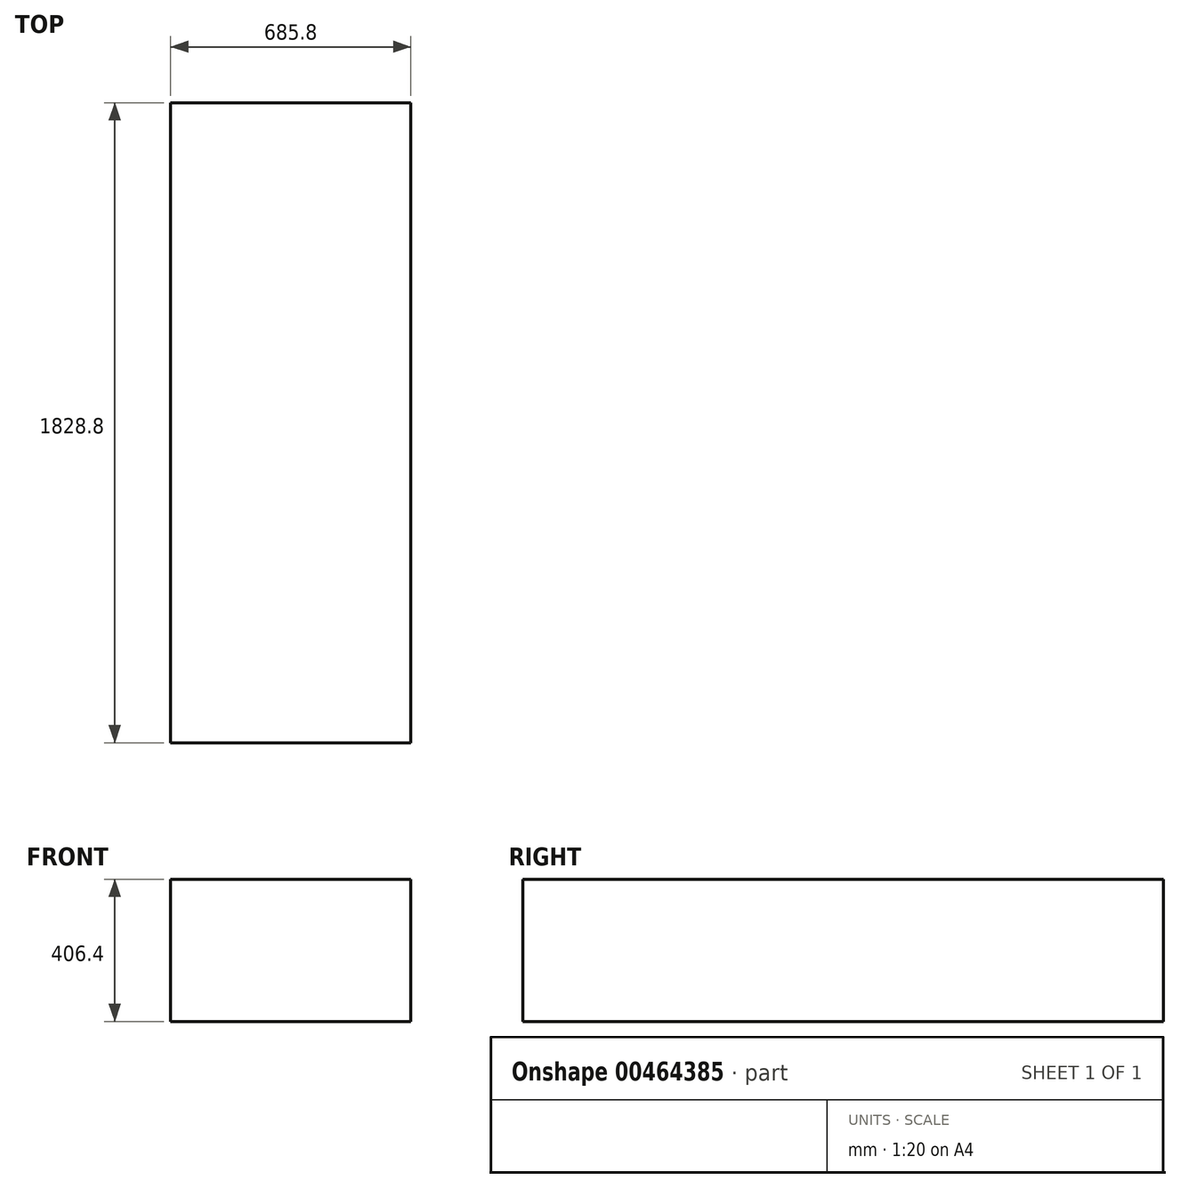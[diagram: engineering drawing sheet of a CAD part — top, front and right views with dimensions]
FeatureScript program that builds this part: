
annotation { "Feature Type Name" : "Feature", "Feature Type Description" : "" }
export const myFeature = defineFeature(function(context is Context, id is Id, definition is map)
    precondition{}
    {
        {
            var Q0;
            Q0=qCreatedBy(makeId("Top.planeOp"),FACE);
            var sketch = newSketch(context, id + "F0", { "sketchPlane" : qUnion([Q0])});
            skLineSegment(sketch, "E0.bottom", {"start": v(-737.4, 0) * mm, "end": v(-51.6, 0) * mm});
            skLineSegment(sketch, "E0.top", {"start": v(-737.4, 1828.8) * mm, "end": v(-51.6, 1828.8) * mm});
            skLineSegment(sketch, "E0.left", {"start": v(-737.4, 0) * mm, "end": v(-737.4, 1828.8) * mm});
            skLineSegment(sketch, "E0.right", {"start": v(-51.6, 0) * mm, "end": v(-51.6, 1828.8) * mm});
            skSolve(sketch);
        }
        {
            var Q0;
            Q0 = qSketchRegion(id + "F0", true);
            extrude(context, id + "F1", {"entities" : qUnion([Q0]), "depth" : 406.4 * mm});
        }
    });
